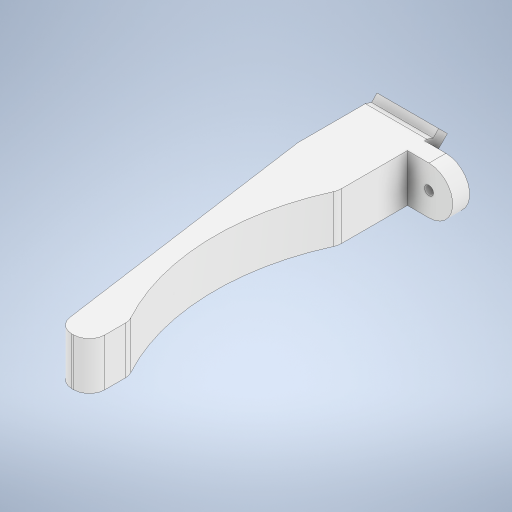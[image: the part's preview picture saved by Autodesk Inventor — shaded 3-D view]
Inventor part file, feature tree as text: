
AUTODESK INVENTOR PART (.ipt)
format: ipt  version: 2024 (Build 280153000, 153)  size: 530,432 bytes
history: native  units: in
note: dims shown in document units (in); Inventor stores cm internally (conversion verified against a paired STEP export)
features: extrude x4, sketch x2, other x1, plane x1, mirror x1, projected_geometry x1, fillet x1
ambient origin geometry x8: Origin, YZ Plane, XZ Plane, XY Plane, X Axis, Y Axis, Z Axis, Center Point
bodies: Solid1 (feature_tree)
feature tree (11):
  other  "Plane1"
  sketch  "Sketch1"  dims[d10=0.0787in d11=0.0787in]
  extrude  "Extrusion1"  Depth=0.0787in
  extrude  "Extrusion2"  Depth=0.3937in
  plane  "Work Plane2"
  extrude  "Extrusion3"  TaperAngle=0.0deg  [1 undecoded]
  extrude  "Extrusion4"  TaperAngle=0.0deg  [1 undecoded]
  mirror  "Mirror1"
  projected_geometry  "Projected Loop1"
  sketch  "Sketch2"  dims[d12=45.0deg d13=0.0414in d14=0.0in d15=0.0in d16=0.035in d17=0.0461in d18=0.0242in d19=0.0108in d20=0.035in d21=0.1969in d22=0.1969in d23=0.0134in d24=0.0423in d25=0.0in d26=0.0in d27=0.3937in d28=0.0in d29=0.0846in d30=0.0846in d31=0.3937in d32=0.0in d33=0.0394in d34=0.0394in d35=0.0in d36=0.0in]
  fillet  "Fillet1"  Radius=0.035in
note: 2 required parameter values undecoded (feature->parameter linkage not recoverable at this tier; creation-order binding heuristic only, values carry confidence <= 0.55)
